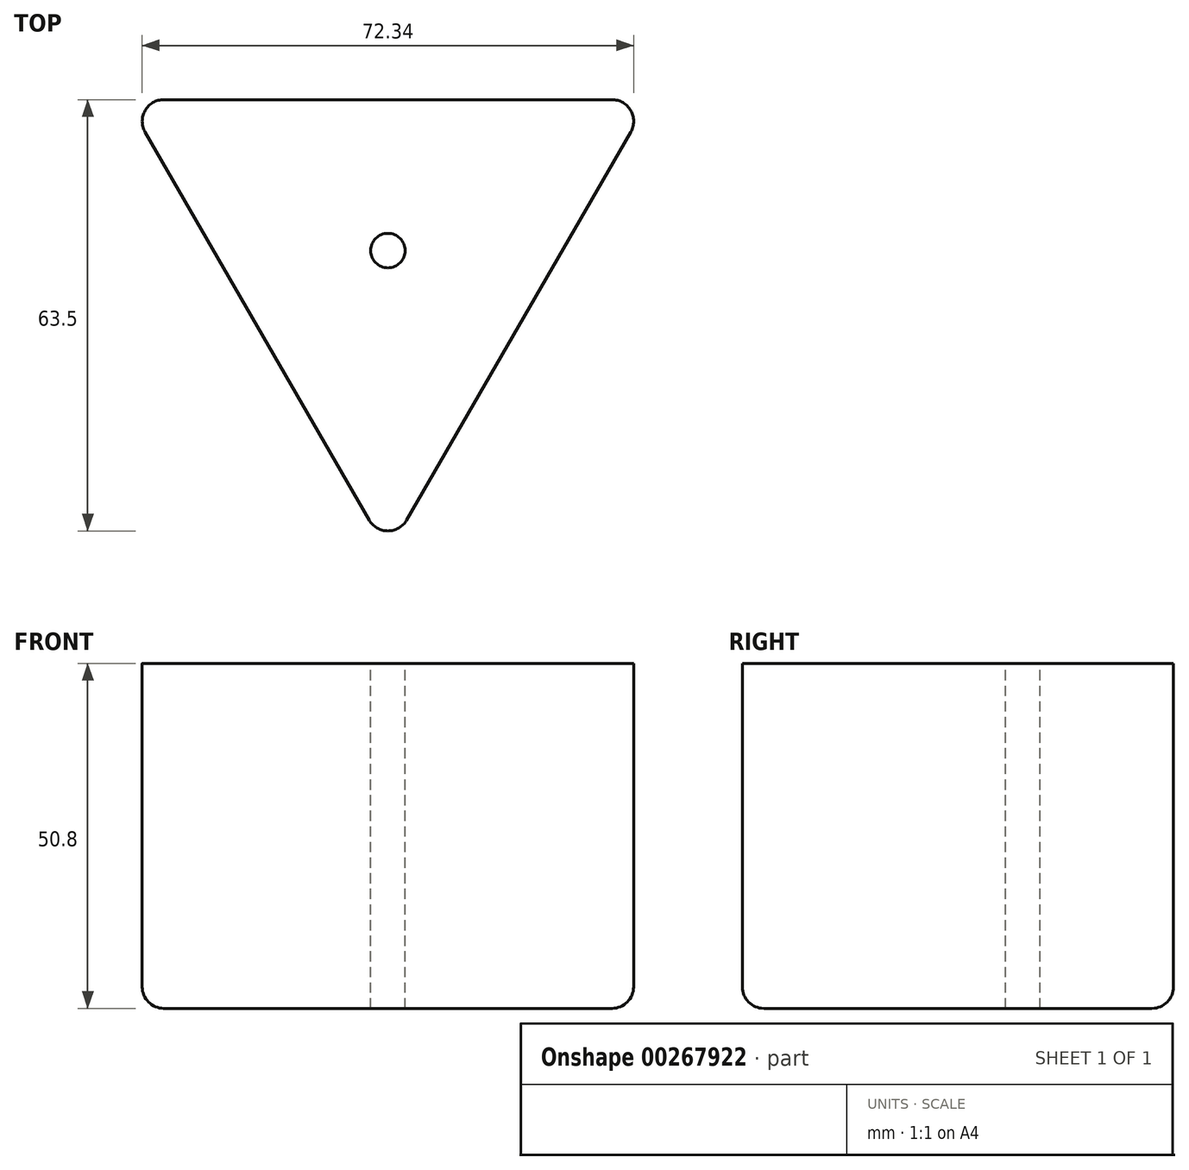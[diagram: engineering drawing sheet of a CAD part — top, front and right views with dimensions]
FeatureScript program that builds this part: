
annotation { "Feature Type Name" : "Feature", "Feature Type Description" : "" }
export const myFeature = defineFeature(function(context is Context, id is Id, definition is map)
    precondition{}
    {
        {
            var Q0;
            Q0=qCreatedBy(makeId("Top.planeOp"),FACE);
            var sketch = newSketch(context, id + "F0", { "sketchPlane" : qUnion([Q0])});
            skCircle(sketch, "E0.cCircle", {"center": v(0, 0) * mm, "radius": 22.23 * mm, "construction": true});
            skLineSegment(sketch, "E0.0", {"start": v(-38.5, 22.22) * mm, "end": v(38.5, 22.23) * mm});
            skLineSegment(sketch, "E0.1", {"start": v(38.5, 22.23) * mm, "end": v(0, -44.45) * mm});
            skLineSegment(sketch, "E0.2", {"start": v(0, -44.45) * mm, "end": v(-38.5, 22.23) * mm});
            skPoint(sketch, "E0.0.midPoint", {"position": v(0, 22.22) * mm});
            skSolve(sketch);
        }
        {
            var Q0;
            Q0 = qSketchRegion(id + "F0", true);
            extrude(context, id + "F1", {"entities" : qUnion([Q0]), "depth" : 50.8 * mm});
        }
        {
            var Q0;
            Q0=makeQuery(id+"F1.opExtrude","SWEPT_EDGE",EDGE,{"disambiguationData":[OSD([sQuery(id+"F0.wireOp",EDGE,"E0.0"),sQuery(id+"F0.wireOp",EDGE,"E0.2")])]});
            var Q1;
            Q1=makeQuery(id+"F1.opExtrude","SWEPT_EDGE",EDGE,{"disambiguationData":[OSD([sQuery(id+"F0.wireOp",EDGE,"E0.1"),sQuery(id+"F0.wireOp",EDGE,"E0.2")])]});
            var Q2;
            Q2=makeQuery(id+"F1.opExtrude","SWEPT_EDGE",EDGE,{"disambiguationData":[OSD([sQuery(id+"F0.wireOp",EDGE,"E0.0"),sQuery(id+"F0.wireOp",EDGE,"E0.1")])]});
            var Q3;
            Q3=makeQuery(id+"F1.opExtrude","CAP_EDGE",EDGE,{"disambiguationData":[OSD([sQuery(id+"F0.wireOp",EDGE,"E0.0")])],"isStart":true});
            var Q4;
            Q4=makeQuery(id+"F1.opExtrude","CAP_EDGE",EDGE,{"disambiguationData":[OSD([sQuery(id+"F0.wireOp",EDGE,"E0.1")])],"isStart":true});
            var Q5;
            Q5=makeQuery(id+"F1.opExtrude","CAP_EDGE",EDGE,{"disambiguationData":[OSD([sQuery(id+"F0.wireOp",EDGE,"E0.2")])],"isStart":true});
            fillet(context, id + "F2", {"entities" : qUnion([Q0, Q1, Q2, Q3, Q4, Q5]), "radius" : 3.17 * mm, "tangentPropagation" : true, "allowEdgeOverflow" : false});
        }
        {
            var Q0;
            Q0=makeQuery(id+"F1.opExtrude","CAP_FACE",FACE,{"disambiguationData":[OSD([sQuery(id+"F0.wireOp",EDGE,"E0.0"),sQuery(id+"F0.wireOp",EDGE,"E0.1"),sQuery(id+"F0.wireOp",EDGE,"E0.2")])],"isStart":false});
            var sketch = newSketch(context, id + "F3", { "sketchPlane" : qUnion([Q0])});
            skCircle(sketch, "E1", {"center": v(0, 0) * mm, "radius": 2.54 * mm});
            skSolve(sketch);
        }
        {
            var Q0;
            Q0 = qSketchRegion(id + "F3", true);
            extrude(context, id + "F4", {"entities" : qUnion([Q0]), "operationType" : NewBodyOperationType.REMOVE, "endBound" : BoundingType.THROUGH_ALL, "oppositeDirection" : true, "depth" : 25.4 * mm});
        }
    });
